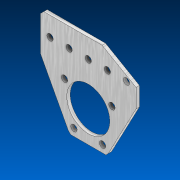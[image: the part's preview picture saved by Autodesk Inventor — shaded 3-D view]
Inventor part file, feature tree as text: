
AUTODESK INVENTOR PART (.ipt)
format: ipt  version: 2022.2 (Build 262287000, 287)  size: 154,624 bytes
history: native  units: in
note: dims shown in document units (in); Inventor stores cm internally (conversion verified against a paired STEP export)
features: extrude x1, sketch x1, other x1
ambient origin geometry x8: Origin, YZ Plane, XZ Plane, XY Plane, X Axis, Y Axis, Z Axis, Center Point
bodies: Solid1 (feature_tree)
feature tree (3):
  extrude  "Extrusion1"  TaperAngle=30.0deg  [1 undecoded]
  sketch  "Sketch1"  dims[d0=0.0in d1=0.0in d2=30.0deg]
  other  "Cut-Extrude1"
note: 1 required parameter value undecoded (feature->parameter linkage not recoverable at this tier; creation-order binding heuristic only, values carry confidence <= 0.55)
